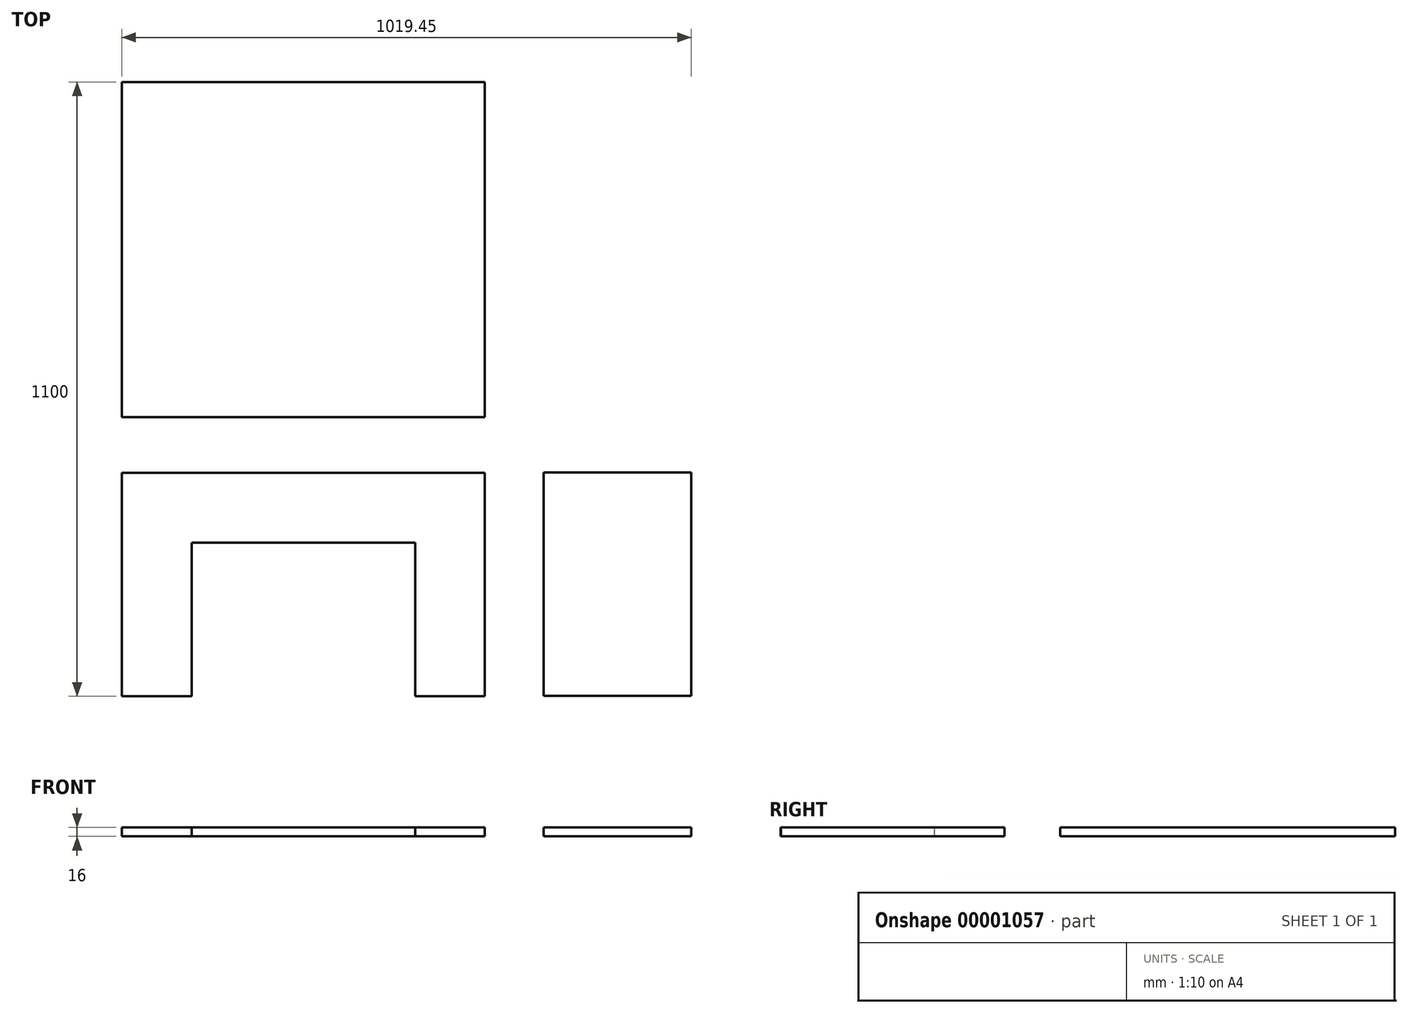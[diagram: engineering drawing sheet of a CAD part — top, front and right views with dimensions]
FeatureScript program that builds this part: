
annotation { "Feature Type Name" : "Feature", "Feature Type Description" : "" }
export const myFeature = defineFeature(function(context is Context, id is Id, definition is map)
    precondition{}
    {
        {
            var Q0;
            Q0=qCreatedBy(makeId("Top.planeOp"),FACE);
            var sketch = newSketch(context, id + "F0", { "sketchPlane" : qUnion([Q0])});
            skLineSegment(sketch, "E0.bottom", {"start": v(0, 0) * mm, "end": v(650, 0) * mm});
            skLineSegment(sketch, "E0.top", {"start": v(0, 600) * mm, "end": v(650, 600) * mm});
            skLineSegment(sketch, "E0.left", {"start": v(0, 0) * mm, "end": v(0, 600) * mm});
            skLineSegment(sketch, "E0.right", {"start": v(650, 0) * mm, "end": v(650, 600) * mm});
            skSolve(sketch);
        }
        {
            var Q0;
            Q0=makeQuery(id+"F0.imprint","IMPRINT",FACE,{"disambiguationData":[TD([[makeQuery(id+"F0.imprint","IMPRINT",EDGE,{"derivedFrom":sQuery(id+"F0.wireOp",EDGE,"E0.bottom")}),1.0]])]});
            var sketch = newSketch(context, id + "F1", { "sketchPlane" : qUnion([Q0])});
            skLineSegment(sketch, "E1.bottom", {"start": v(0, -500) * mm, "end": v(125, -500) * mm});
            skLineSegment(sketch, "E1.top", {"start": v(0, -100) * mm, "end": v(650, -100) * mm});
            skLineSegment(sketch, "E1.left", {"start": v(0, -500) * mm, "end": v(0, -100) * mm});
            skLineSegment(sketch, "E1.right", {"start": v(650, -500) * mm, "end": v(650, -100) * mm});
            skLineSegment(sketch, "E2.top", {"start": v(125, -225) * mm, "end": v(525, -225) * mm});
            skLineSegment(sketch, "E2.left", {"start": v(125, -500) * mm, "end": v(125, -225) * mm});
            skLineSegment(sketch, "E2.right", {"start": v(525, -500) * mm, "end": v(525, -225) * mm});
            skLineSegment(sketch, "E3.trimOffspring", {"start": v(525, -500) * mm, "end": v(650, -500) * mm});
            skLineSegment(sketch, "E4", {"start": v(525, -225) * mm, "end": v(525, -100) * mm, "construction": true});
            skSolve(sketch);
        }
        {
            var Q0;
            Q0=makeQuery(id+"F0.imprint","IMPRINT",FACE,{"disambiguationData":[TD([[makeQuery(id+"F0.imprint","IMPRINT",EDGE,{"derivedFrom":sQuery(id+"F0.wireOp",EDGE,"E0.bottom")}),1.0]])]});
            var sketch = newSketch(context, id + "F2", { "sketchPlane" : qUnion([Q0])});
            skLineSegment(sketch, "E5.bottom", {"start": v(755.45, -99.39) * mm, "end": v(1019.45, -99.39) * mm});
            skLineSegment(sketch, "E5.top", {"start": v(755.45, -499.39) * mm, "end": v(1019.45, -499.39) * mm});
            skLineSegment(sketch, "E5.left", {"start": v(755.45, -99.39) * mm, "end": v(755.45, -499.39) * mm});
            skLineSegment(sketch, "E5.right", {"start": v(1019.45, -99.39) * mm, "end": v(1019.45, -499.39) * mm});
            skSolve(sketch);
        }
        {
            var Q0;
            Q0=makeQuery(id+"FPVNH45VRz3vqj1_0.opExtrude","CAP_FACE",FACE,{"disambiguationData":[OSD([sQuery(id+"F0.wireOp",EDGE,"E0.bottom"),sQuery(id+"F0.wireOp",EDGE,"E0.top"),sQuery(id+"F0.wireOp",EDGE,"E0.left"),sQuery(id+"F0.wireOp",EDGE,"E0.right")])],"isStart":false});
            var sketch = newSketch(context, id + "F3", { "sketchPlane" : qUnion([Q0])});
            skLineSegment(sketch, "E6.bottom", {"start": v(749.52, 359.78) * mm, "end": v(1109.52, 359.78) * mm});
            skLineSegment(sketch, "E6.top", {"start": v(749.52, 85.78) * mm, "end": v(1109.52, 85.78) * mm});
            skLineSegment(sketch, "E6.left", {"start": v(749.52, 359.78) * mm, "end": v(749.52, 85.78) * mm});
            skLineSegment(sketch, "E6.right", {"start": v(1109.52, 359.78) * mm, "end": v(1109.52, 85.78) * mm});
            skSolve(sketch);
        }
        {
            var Q0;
            Q0=makeQuery(id+"F0.imprint","IMPRINT",FACE,{"disambiguationData":[TD([[makeQuery(id+"F0.imprint","IMPRINT",EDGE,{"derivedFrom":sQuery(id+"F0.wireOp",EDGE,"E0.bottom")}),1.0]])]});
            var Q1;
            Q1=makeQuery(id+"F1.imprint","IMPRINT",FACE,{"disambiguationData":[TD([[makeQuery(id+"F1.imprint","IMPRINT",EDGE,{"derivedFrom":sQuery(id+"F1.wireOp",EDGE,"E1.bottom")}),1.0]])]});
            var Q2;
            Q2=makeQuery(id+"F2.imprint","IMPRINT",FACE,{"disambiguationData":[TD([[makeQuery(id+"F2.imprint","IMPRINT",EDGE,{"derivedFrom":sQuery(id+"F2.wireOp",EDGE,"E5.bottom")}),-1.0]])]});
            var Q3;
            Q3=makeQuery(id+"F3.imprint","IMPRINT",FACE,{"disambiguationData":[TD([[makeQuery(id+"F3.imprint","IMPRINT",EDGE,{"derivedFrom":sQuery(id+"F3.wireOp",EDGE,"E6.bottom")}),-1.0]])]});
            extrude(context, id + "F4", {"entities" : qUnion([Q0, Q1, Q2, Q3]), "depth" : 16 * mm});
        }
    });
